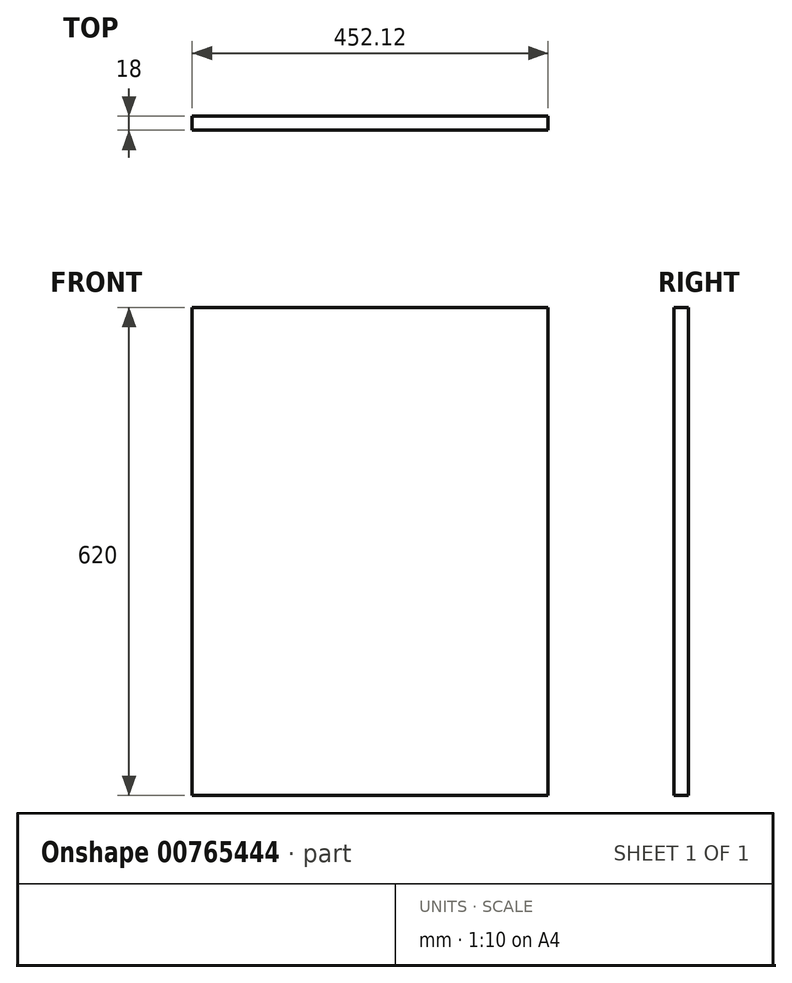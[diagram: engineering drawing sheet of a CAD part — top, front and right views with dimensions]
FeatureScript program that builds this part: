
annotation { "Feature Type Name" : "Feature", "Feature Type Description" : "" }
export const myFeature = defineFeature(function(context is Context, id is Id, definition is map)
    precondition{}
    {
        {
            var Q0;
            Q0=qCreatedBy(makeId("Front.planeOp"),FACE);
            var sketch = newSketch(context, id + "F0", { "sketchPlane" : qUnion([Q0])});
            skLineSegment(sketch, "E0.bottom", {"start": v(-226.06, -310) * mm, "end": v(226.06, -310) * mm});
            skLineSegment(sketch, "E0.top", {"start": v(-226.06, 310) * mm, "end": v(226.06, 310) * mm});
            skLineSegment(sketch, "E0.left", {"start": v(-226.06, -310) * mm, "end": v(-226.06, 310) * mm});
            skLineSegment(sketch, "E0.right", {"start": v(226.06, -310) * mm, "end": v(226.06, 310) * mm});
            skPoint(sketch, "E0.middle", {"position": v(0, 0) * mm});
            skSolve(sketch);
        }
        {
            var Q0;
            Q0 = qSketchRegion(id + "F0", true);
            extrude(context, id + "F1", {"entities" : qUnion([Q0]), "depth" : 18 * mm, "offsetDistance" : 25 * mm});
        }
    });
